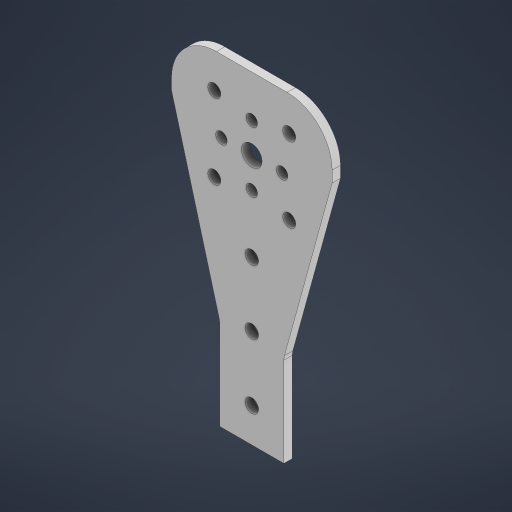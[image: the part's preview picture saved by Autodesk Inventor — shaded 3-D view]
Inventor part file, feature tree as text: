
AUTODESK INVENTOR PART (.ipt)
format: ipt  version: 2024 (Build 280153000, 153)  size: 251,904 bytes
history: native  units: in
note: dims shown in document units (in); Inventor stores cm internally (conversion verified against a paired STEP export)
features: fillet x3, sketch x3, hole x2, pattern_circular x2, extrude x1
ambient origin geometry x8: Origin, YZ Plane, XZ Plane, XY Plane, X Axis, Y Axis, Z Axis, Center Point
bodies: Solid1 (feature_tree)
feature tree (11):
  extrude  "Extrusion1"  Depth=2.5in
  fillet  "Fillet11"  Radius=0.209in
  fillet  "Fillet12"  Radius=1.125in
  hole  "Hole1"  [1 undecoded]
  pattern_circular  "Circular Pattern1"  [2 undecoded]
  hole  "Hole2"  [1 undecoded]
  pattern_circular  "Circular Pattern2"  [2 undecoded]
  fillet  "Fillet16"  [1 undecoded]
  sketch  "Sketch1"  dims[d0=2.5in d2=0.3189in d3=0.209in d5=1.125in]
  sketch  "Sketch3"  dims[d10=0.13in d11=0.0in d22=0.7in]
  sketch  "Sketch4"  dims[d23=0.7in d26=1.2598in d27=0.6299in d28=0.9449in d29=0.177in d30=0.75in d31=0.37in d32=0.25in d33=90.0deg d34=0.559in d35=0.8108in d36=90.0deg d37=1.5748in d38=360.0deg d40=0.9449in d41=1.2598in d42=1.65in d43=0.201in d44=0.432in d45=0.385in d46=0.25in d47=0.5635in d48=0.64in d49=0.8108in d50=3.25in d51=1.5748in d52=360.0deg d54=0.209in d55=2.5in d58=45.0deg d59=1.0in d60=1.0in d61=1.0in d63=0.25in d16=0.0in d17=0.0in d18=0.0in d19=0.0in d20=0.0in d21=0.0in]
note: 7 required parameter values undecoded (feature->parameter linkage not recoverable at this tier; creation-order binding heuristic only, values carry confidence <= 0.55)
